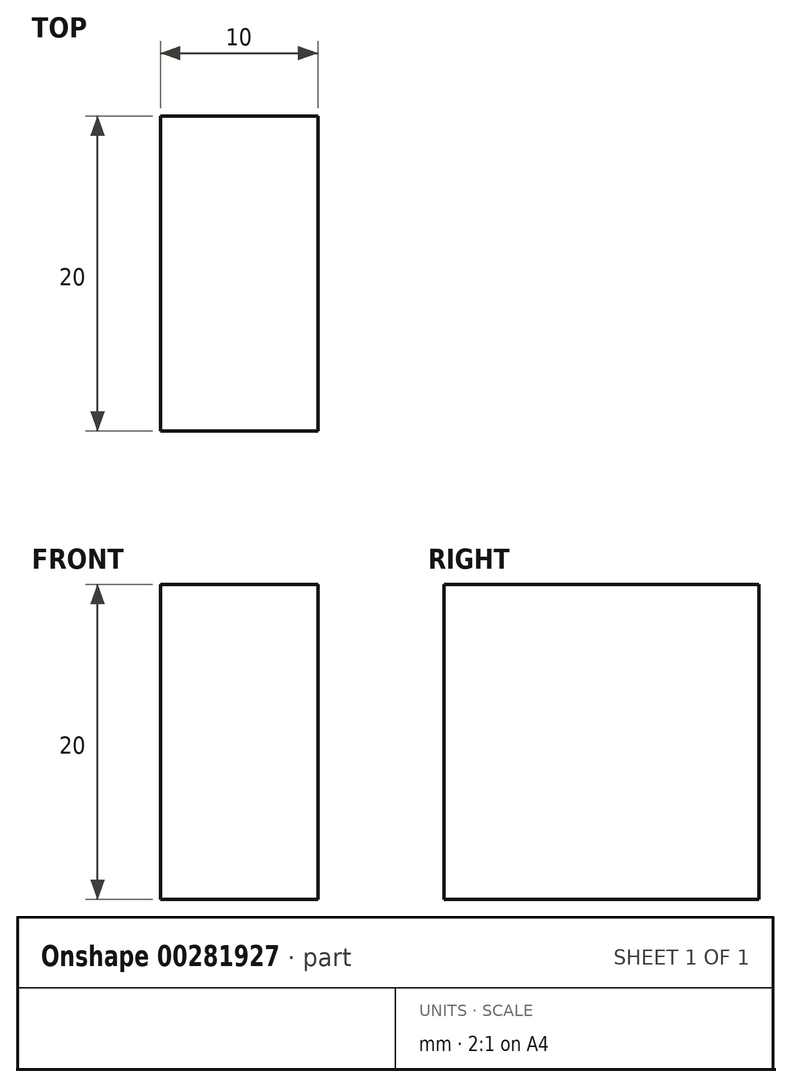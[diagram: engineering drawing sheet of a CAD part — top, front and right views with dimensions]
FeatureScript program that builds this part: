
annotation { "Feature Type Name" : "Feature", "Feature Type Description" : "" }
export const myFeature = defineFeature(function(context is Context, id is Id, definition is map)
    precondition{}
    {
        {
            var Q0;
            Q0=qCreatedBy(makeId("Front.planeOp"),FACE);
            var sketch = newSketch(context, id + "F0", { "sketchPlane" : qUnion([Q0])});
            skLineSegment(sketch, "E0.bottom", {"start": v(0, 0) * mm, "end": v(10, 0) * mm});
            skLineSegment(sketch, "E0.top", {"start": v(0, -20) * mm, "end": v(10, -20) * mm});
            skLineSegment(sketch, "E0.left", {"start": v(0, 0) * mm, "end": v(0, -20) * mm});
            skLineSegment(sketch, "E0.right", {"start": v(10, 0) * mm, "end": v(10, -20) * mm});
            skSolve(sketch);
        }
        {
            var Q0;
            Q0 = qSketchRegion(id + "F0", true);
            extrude(context, id + "F1", {"entities" : qUnion([Q0]), "depth" : 20 * mm});
        }
    });
